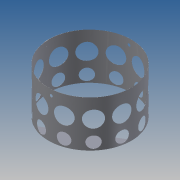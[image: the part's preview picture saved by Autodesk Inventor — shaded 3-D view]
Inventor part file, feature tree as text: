
AUTODESK INVENTOR PART (.ipt)
format: ipt  version: 2014 SP1 (Build 180222100, 222)  size: 911,872 bytes
history: native  units: in
note: dims shown in document units (in); Inventor stores cm internally (conversion verified against a paired STEP export)
features: sketch x6, hole x4, sheet_metal_op x2, extrude x2, other x2, thicken_offset x1
ambient origin geometry x8: Origin, YZ Plane, XZ Plane, XY Plane, X Axis, Y Axis, Z Axis, Center Point
bodies: Solid1 (feature_tree)
feature tree (17):
  thicken_offset  "Thicken1"
  sheet_metal_op  "Unfold4"
  hole  "spars"  [1 undecoded]
  hole  "supports"  [1 undecoded]
  hole  "rivets"  [1 undecoded]
  hole  "rebar"  [1 undecoded]
  sheet_metal_op  "Refold2"
  extrude  "__centeringRing"  Depth=0.8108in
  sketch  "Sketch1"  dims[d0=0.0in d1=144.2386in d2=10.0in d3=0.0in]
  other  "2D Equation Curve1"
  other  "Srf1"
  sketch  "Sketch2"  dims[d4=0.0394in d5=0.0394in]
  sketch  "Sketch3"  dims[d6=3.622in d7=5.9055in]
  sketch  "Sketch7"  dims[d8=2.905in d9=4.7244in d11=4.7124in d12=0.3937in d14=1.0in]
  sketch  "Sketch9"  dims[d16=3.5827in d17=0.75in d18=0.375in d19=0.25in d20=0.5635in d21=0.0394in d22=0.8108in]
  sketch  "Sketch10"  dims[d23=2.4803in d24=1.5748in d25=4.7244in d27=4.7125in d28=0.3937in d30=1.0in d32=2.905in d33=2.5197in d34=0.75in d35=0.375in d36=0.25in d37=0.5635in d38=0.0394in d39=0.8108in d68=0.125in d69=1.0in d70=0.5in d71=1.9685in d73=2.0in d74=0.3937in d76=1.0in d78=1.0in d79=0.0394in d80=0.75in d81=0.375in d82=0.25in d83=0.5635in d84=0.0394in d85=0.8108in d88=0.3937in d89=0.5906in d90=0.75in d91=0.375in d92=0.25in d93=0.5635in d94=0.0394in d95=0.8108in d97=18.0in d98=0.0394in d99=19.685in d100=0.0in d101=2.8386in d102=1.2559in]
  extrude  "ExtrusionSrf1"  Depth=1.5748in
note: 4 required parameter values undecoded (feature->parameter linkage not recoverable at this tier; creation-order binding heuristic only, values carry confidence <= 0.55)
